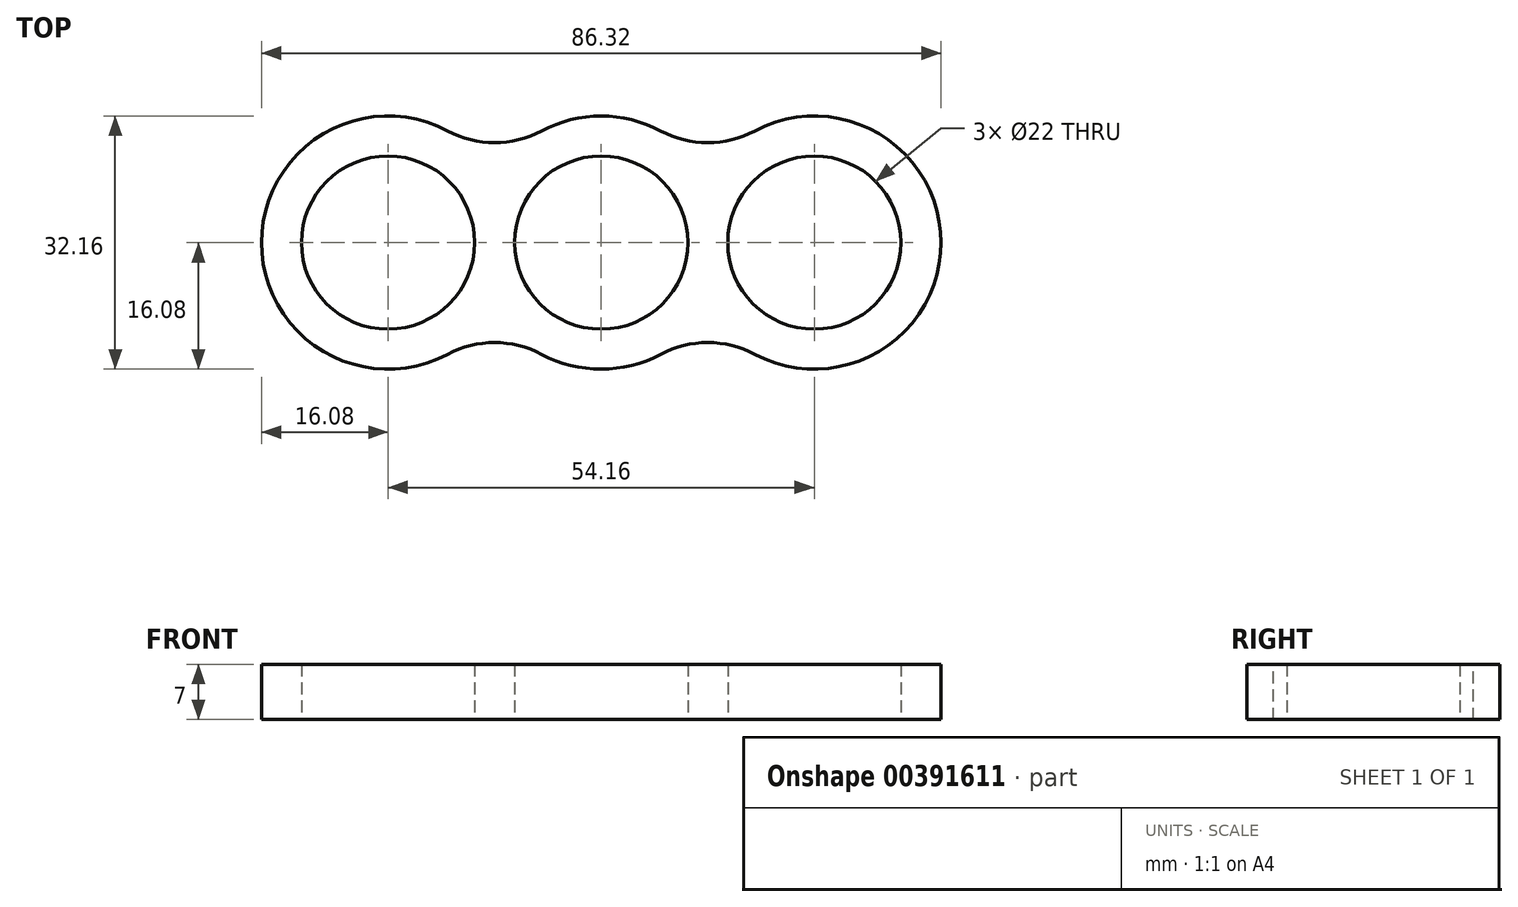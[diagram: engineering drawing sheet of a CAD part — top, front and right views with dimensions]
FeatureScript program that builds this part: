
annotation { "Feature Type Name" : "Feature", "Feature Type Description" : "" }
export const myFeature = defineFeature(function(context is Context, id is Id, definition is map)
    precondition{}
    {
        {
            var Q0;
            Q0=qCreatedBy(makeId("Top.planeOp"),FACE);
            var sketch = newSketch(context, id + "F0", { "sketchPlane" : qUnion([Q0])});
            skArc(sketch, "E0", {"start": v(0, 11) * mm, "mid": v(-11, 0) * mm, "end": v(0, -11) * mm});
            skCircle(sketch, "E1", {"center": v(-27.08, 0) * mm, "radius": 11 * mm});
            skPoint(sketch, "E2.orphan", {"position": v(-43.16, 16.08) * mm});
            skPoint(sketch, "E3.orphan", {"position": v(-43.16, -16.08) * mm});
            skPoint(sketch, "E4.start.orphan", {"position": v(-43.16, 0) * mm});
            skArc(sketch, "E5", {"start": v(-27.08, -16.08) * mm, "mid": v(-43.16, 0) * mm, "end": v(-27.08, 16.08) * mm});
            skPoint(sketch, "E6.orphan", {"position": v(-16.08, 0) * mm});
            skPoint(sketch, "E7.orphan", {"position": v(-11, 0) * mm});
            skCircle(sketch, "E8.MirrorC", {"center": v(27.08, 0) * mm, "radius": 11 * mm});
            skPoint(sketch, "E9.MirrorP", {"position": v(11, 0) * mm});
            skPoint(sketch, "E10.MirrorP", {"position": v(16.08, 0) * mm});
            skPoint(sketch, "E11.MirrorP", {"position": v(43.16, 16.08) * mm});
            skArc(sketch, "E12.MirrorCS", {"start": v(27.08, -16.08) * mm, "mid": v(43.16, 0) * mm, "end": v(27.08, 16.08) * mm});
            skArc(sketch, "E13.MirrorCS", {"start": v(0, 11) * mm, "mid": v(11, 0) * mm, "end": v(0, -11) * mm});
            skPoint(sketch, "E14.MirrorP", {"position": v(43.16, 0) * mm});
            skPoint(sketch, "E15.MirrorP", {"position": v(43.16, -16.08) * mm});
            skPoint(sketch, "E16.end.orphan", {"position": v(-13.54, 8.67) * mm});
            skPoint(sketch, "E16.start.orphan", {"position": v(0, 16.08) * mm});
            skPoint(sketch, "E17.MirrorCS.end.orphan", {"position": v(13.54, 8.67) * mm});
            skPoint(sketch, "E18.MirrorCS.start.orphan", {"position": v(0, -16.08) * mm});
            skPoint(sketch, "E19.MirrorCS.end.orphan", {"position": v(13.54, -8.67) * mm});
            skPoint(sketch, "E20.end.orphan", {"position": v(-13.54, -8.67) * mm});
            skArc(sketch, "E21", {"start": v(-27.08, 16.08) * mm, "mid": v(-19.36, 14.1) * mm, "end": v(-13.54, 8.67) * mm});
            skArc(sketch, "E22", {"start": v(-13.54, 8.67) * mm, "mid": v(-7.72, 14.1) * mm, "end": v(0, 16.08) * mm});
            skArc(sketch, "E23", {"start": v(-13.54, -8.67) * mm, "mid": v(-7.72, -14.1) * mm, "end": v(0, -16.08) * mm});
            skArc(sketch, "E24", {"start": v(-27.08, -16.08) * mm, "mid": v(-19.36, -14.1) * mm, "end": v(-13.54, -8.67) * mm});
            skArc(sketch, "E25", {"start": v(0, 16.08) * mm, "mid": v(7.72, 14.1) * mm, "end": v(13.54, 8.67) * mm});
            skArc(sketch, "E26", {"start": v(27.08, 16.08) * mm, "mid": v(19.36, 14.1) * mm, "end": v(13.54, 8.67) * mm});
            skArc(sketch, "E27", {"start": v(0, -16.08) * mm, "mid": v(7.72, -14.1) * mm, "end": v(13.54, -8.67) * mm});
            skArc(sketch, "E28", {"start": v(13.54, -8.67) * mm, "mid": v(19.36, -14.1) * mm, "end": v(27.08, -16.08) * mm});
            skSolve(sketch);
        }
        {
            var Q0;
            Q0=qSketchRegion(id+"F0",true);
            extrude(context, id + "F1", {"entities" : qUnion([Q0]), "depth" : 7 * mm});
        }
        {
            var Q0;
            Q0=makeQuery(id+"F1.opExtrude","SWEPT_EDGE",EDGE,{"disambiguationData":[OSD([sQuery(id+"F0.wireOp",EDGE,"E23"),sQuery(id+"F0.wireOp",EDGE,"E24")])]});
            var Q1;
            Q1=makeQuery(id+"F1.opExtrude","SWEPT_EDGE",EDGE,{"disambiguationData":[OSD([sQuery(id+"F0.wireOp",EDGE,"E27"),sQuery(id+"F0.wireOp",EDGE,"E28")])]});
            var Q2;
            Q2=makeQuery(id+"F1.opExtrude","SWEPT_EDGE",EDGE,{"disambiguationData":[OSD([sQuery(id+"F0.wireOp",EDGE,"E21"),sQuery(id+"F0.wireOp",EDGE,"E22")])]});
            var Q3;
            Q3=makeQuery(id+"F1.opExtrude","SWEPT_EDGE",EDGE,{"disambiguationData":[OSD([sQuery(id+"F0.wireOp",EDGE,"E25"),sQuery(id+"F0.wireOp",EDGE,"E26")])]});
            fillet(context, id + "F2", {"entities" : qUnion([Q0, Q1, Q2, Q3]), "radius" : 12.7 * mm, "tangentPropagation" : true, "allowEdgeOverflow" : false});
        }
    });
